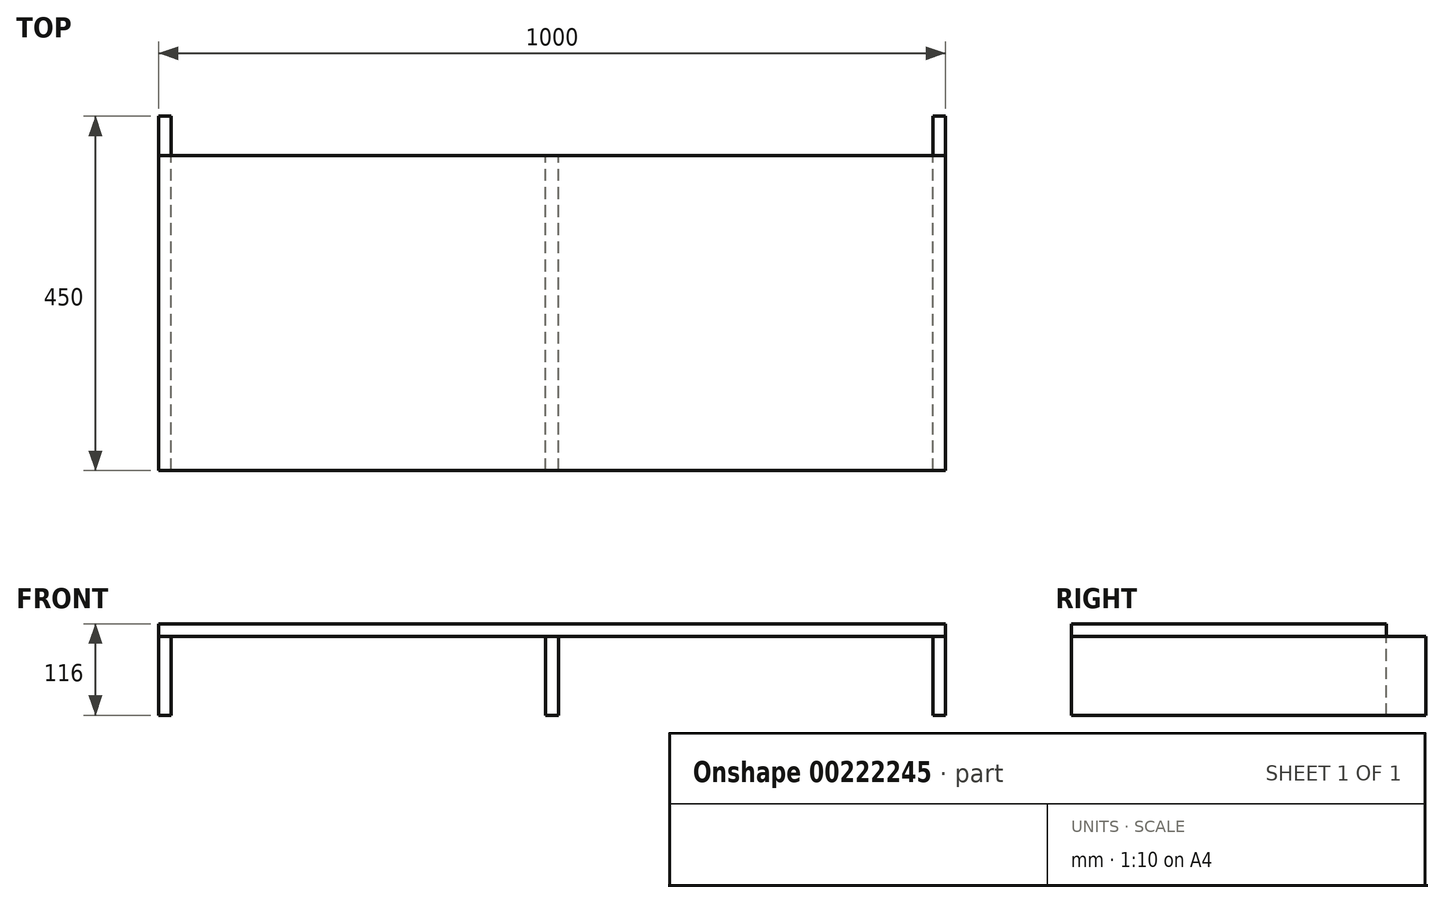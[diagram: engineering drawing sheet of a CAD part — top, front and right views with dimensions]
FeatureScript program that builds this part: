
annotation { "Feature Type Name" : "Feature", "Feature Type Description" : "" }
export const myFeature = defineFeature(function(context is Context, id is Id, definition is map)
    precondition{}
    {
        {
            var Q0;
            Q0=qCreatedBy(makeId("Top.planeOp"),FACE);
            var sketch = newSketch(context, id + "F0", { "sketchPlane" : qUnion([Q0])});
            skLineSegment(sketch, "E0.bottom", {"start": v(500, 200) * mm, "end": v(-500, 200) * mm});
            skLineSegment(sketch, "E0.top", {"start": v(500, -200) * mm, "end": v(-500, -200) * mm});
            skLineSegment(sketch, "E0.left", {"start": v(500, 200) * mm, "end": v(500, -200) * mm});
            skLineSegment(sketch, "E0.right", {"start": v(-500, 200) * mm, "end": v(-500, -200) * mm});
            skPoint(sketch, "E0.middle", {"position": v(0, 0) * mm});
            skSolve(sketch);
        }
        {
            var Q0;
            Q0=makeQuery(id+"F0.imprint","IMPRINT",FACE,{"disambiguationData":[TD([[makeQuery(id+"F0.imprint","IMPRINT",EDGE,{"derivedFrom":sQuery(id+"F0.wireOp",EDGE,"E0.bottom")}),1.0]])]});
            extrude(context, id + "F1", {"entities" : qUnion([Q0]), "oppositeDirection" : true, "depth" : 16 * mm});
        }
        {
            var Q0;
            Q0=makeQuery(id+"F1.opExtrude","SWEPT_FACE",FACE,{"disambiguationData":[OSD([sQuery(id+"F0.wireOp",EDGE,"E0.left")])]});
            cPlane(context, id + "F2", {"entities" : qUnion([Q0]), "cplaneType" : CPlaneType.OFFSET, "offset" : 0 * mm, "width" : 150 * mm, "height" : 150 * mm});
        }
        {
            var Q0;
            Q0=qCreatedBy(id+"F2.planeOp",FACE);
            var sketch = newSketch(context, id + "F3", { "sketchPlane" : qUnion([Q0])});
            skLineSegment(sketch, "E1.bottom", {"start": v(-200, -16) * mm, "end": v(250, -16) * mm});
            skLineSegment(sketch, "E1.top", {"start": v(-200, -116) * mm, "end": v(250, -116) * mm});
            skLineSegment(sketch, "E1.left", {"start": v(-200, -16) * mm, "end": v(-200, -116) * mm});
            skLineSegment(sketch, "E1.right", {"start": v(250, -16) * mm, "end": v(250, -116) * mm});
            skSolve(sketch);
        }
        {
            var Q0;
            Q0=makeQuery(id+"F3.imprint","IMPRINT",FACE,{"disambiguationData":[TD([[makeQuery(id+"F3.imprint","IMPRINT",EDGE,{"derivedFrom":sQuery(id+"F3.wireOp",EDGE,"E1.bottom")}),-1.0]])]});
            extrude(context, id + "F4", {"entities" : qUnion([Q0]), "oppositeDirection" : true, "depth" : 16 * mm});
        }
        {
            var Q0;
            Q0=makeQuery(id+"F4.opExtrude","SWEPT_BODY",BODY,{"disambiguationData":[OSD([sQuery(id+"F3.wireOp",EDGE,"E1.bottom"),sQuery(id+"F3.wireOp",EDGE,"E1.top"),sQuery(id+"F3.wireOp",EDGE,"E1.left"),sQuery(id+"F3.wireOp",EDGE,"E1.right")])]});
            var Q1;
            Q1=qCreatedBy(makeId("Right.planeOp"),FACE);
            mirror(context, id + "F5", {"entities" : qUnion([Q0]), "mirrorPlane" : qUnion([Q1])});
        }
        {
            var Q0;
            Q0=qCreatedBy(makeId("Right.planeOp"),FACE);
            var sketch = newSketch(context, id + "F6", { "sketchPlane" : qUnion([Q0])});
            skLineSegment(sketch, "E2.bottom", {"start": v(-200, -116) * mm, "end": v(200, -116) * mm});
            skLineSegment(sketch, "E2.top", {"start": v(-200, -16) * mm, "end": v(200, -16) * mm});
            skLineSegment(sketch, "E2.left", {"start": v(-200, -116) * mm, "end": v(-200, -16) * mm});
            skLineSegment(sketch, "E2.right", {"start": v(200, -116) * mm, "end": v(200, -16) * mm});
            skPoint(sketch, "E2.middle", {"position": v(0, -66) * mm});
            skSolve(sketch);
        }
        {
            var Q0;
            Q0=makeQuery(id+"F6.imprint","IMPRINT",FACE,{"disambiguationData":[TD([[makeQuery(id+"F6.imprint","IMPRINT",EDGE,{"derivedFrom":sQuery(id+"F6.wireOp",EDGE,"E2.bottom")}),1.0]])]});
            extrude(context, id + "F7", {"entities" : qUnion([Q0]), "depth" : 8 * mm, "hasSecondDirection" : true, "secondDirectionOppositeDirection" : true, "secondDirectionDepth" : 8 * mm});
        }
    });
